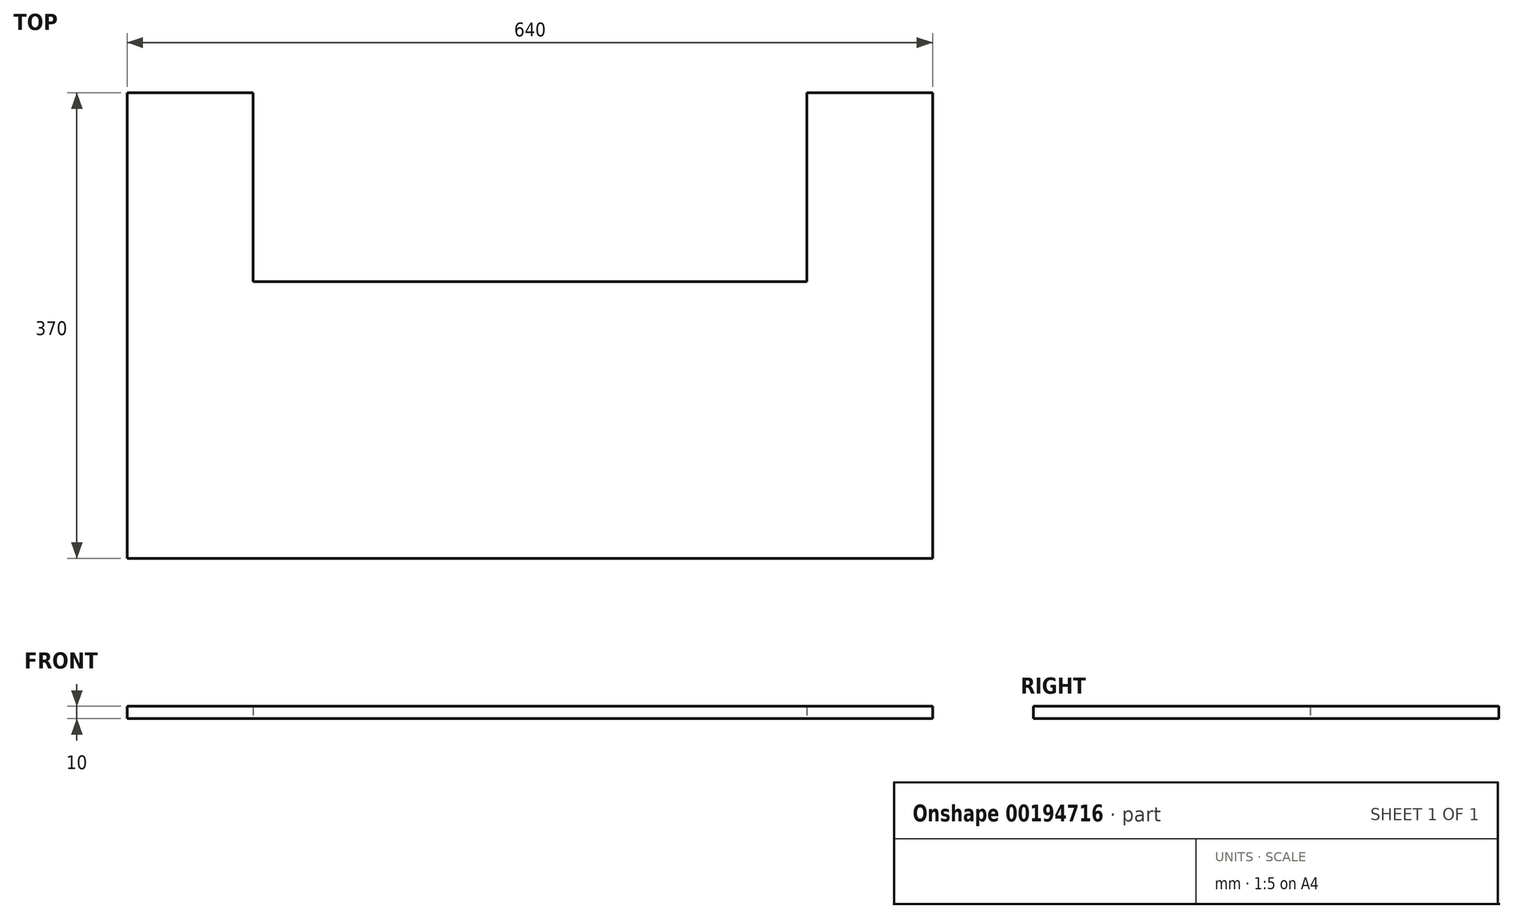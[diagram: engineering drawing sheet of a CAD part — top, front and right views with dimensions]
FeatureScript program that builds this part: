
annotation { "Feature Type Name" : "Feature", "Feature Type Description" : "" }
export const myFeature = defineFeature(function(context is Context, id is Id, definition is map)
    precondition{}
    {
        {
            var Q0;
            Q0=qCreatedBy(makeId("Top.planeOp"),FACE);
            var sketch = newSketch(context, id + "F0", { "sketchPlane" : qUnion([Q0])});
            skLineSegment(sketch, "E0.bottom", {"start": v(320, 185) * mm, "end": v(-320, 185) * mm});
            skLineSegment(sketch, "E0.top", {"start": v(320, -185) * mm, "end": v(-320, -185) * mm});
            skLineSegment(sketch, "E0.left", {"start": v(320, 185) * mm, "end": v(320, -185) * mm});
            skLineSegment(sketch, "E0.right", {"start": v(-320, 185) * mm, "end": v(-320, -185) * mm});
            skPoint(sketch, "E0.middle", {"position": v(0, 0) * mm});
            skLineSegment(sketch, "E1", {"start": v(-220, 185) * mm, "end": v(-220, 35) * mm});
            skLineSegment(sketch, "E2", {"start": v(-220, 35) * mm, "end": v(220, 35) * mm});
            skLineSegment(sketch, "E3", {"start": v(220, 35) * mm, "end": v(220, 185) * mm});
            skSolve(sketch);
        }
        {
            var Q0;
            Q0=makeQuery(id+"F0.imprint","IMPRINT",FACE,{"disambiguationData":[TD([[makeQuery(id+"F0.imprint","IMPRINT",EDGE,{"derivedFrom":sQuery(id+"F0.wireOp",EDGE,"E0.top")}),-1.0]])]});
            extrude(context, id + "F1", {"entities" : qUnion([Q0]), "depth" : 10 * mm});
        }
    });
